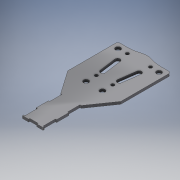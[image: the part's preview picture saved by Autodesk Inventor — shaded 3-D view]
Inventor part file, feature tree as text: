
AUTODESK INVENTOR PART (.ipt)
format: ipt  version: 2017 (Build 210142000, 142)  size: 156,672 bytes
history: native  units: mm
features: other x3, extrude x1, sketch x1, reference x1
ambient origin geometry x8: Origin, YZ Plane, XZ Plane, XY Plane, X Axis, Y Axis, Z Axis, Center Point
bodies: Solid1 (feature_tree)
feature tree (6):
  extrude  "Extrusion1"  Depth=3.0mm
  sketch  "Sketch1"  dims[d0=3.0mm d1=3.0mm d2=3.0mm d3=3.0mm d4=6.0mm d5=0.0mm]
  reference  "Reference1"
  other  "<userpath>\Dropbox\Work\Project\Inventor\Base Assembly.iam"
  other  "Base Assembly.iam"
  other  "Arm - stand plate:1"
